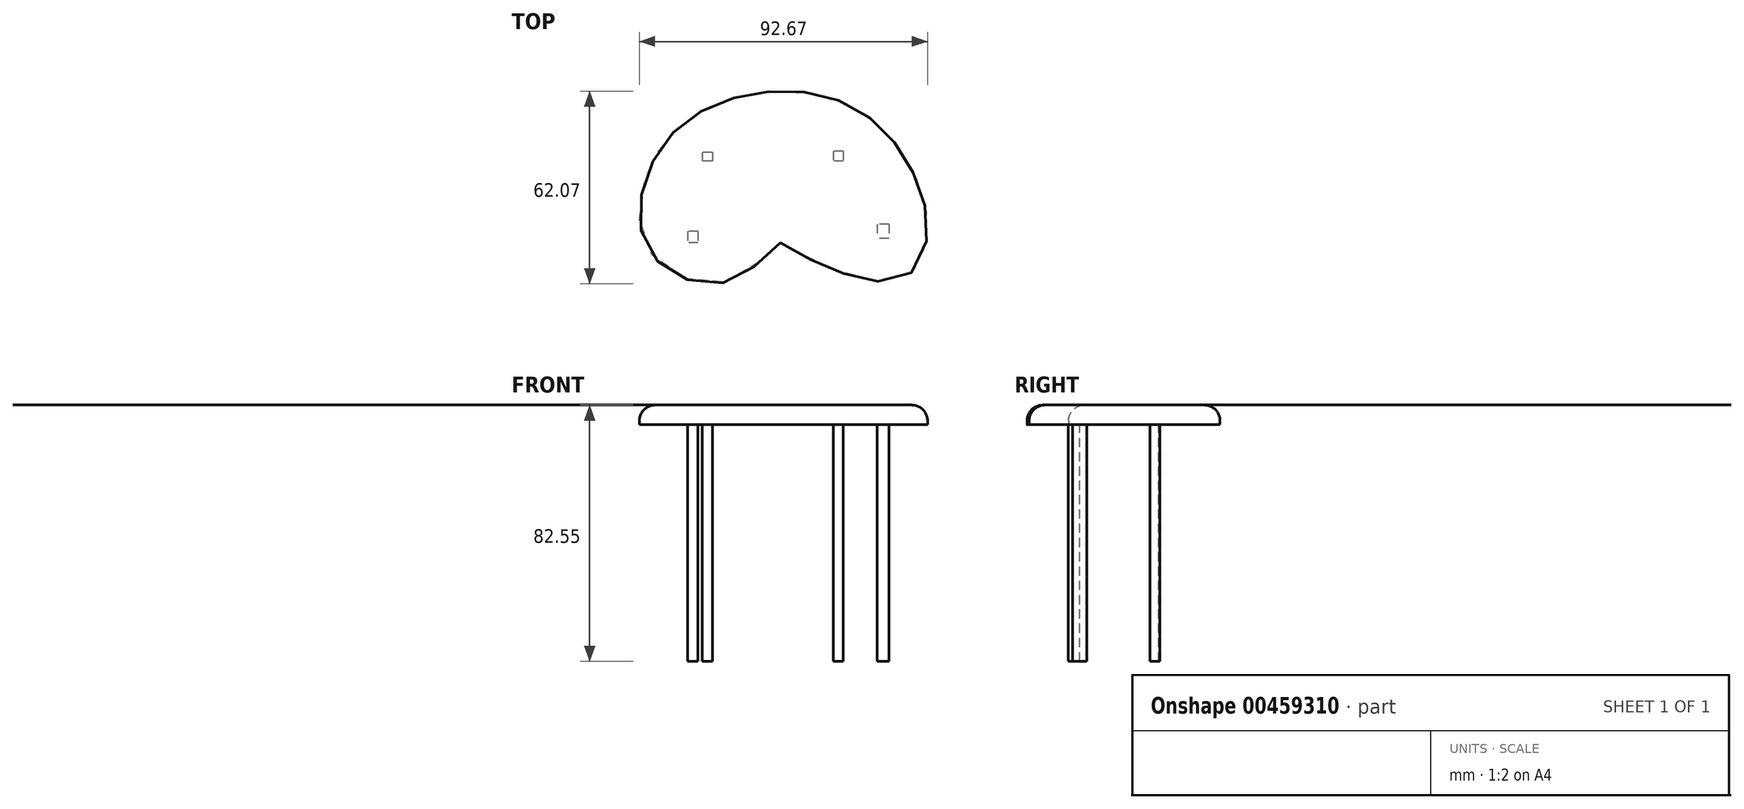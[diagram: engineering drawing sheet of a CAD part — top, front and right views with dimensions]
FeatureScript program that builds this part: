
annotation { "Feature Type Name" : "Feature", "Feature Type Description" : "" }
export const myFeature = defineFeature(function(context is Context, id is Id, definition is map)
    precondition{}
    {
        {
            var Q0;
            Q0=qCreatedBy(makeId("Top.planeOp"),FACE);
            var sketch = newSketch(context, id + "F0", { "sketchPlane" : qUnion([Q0])});
            skFitSpline(sketch, "E0", {"points": [v(0, -6.05) * mm, v(-16.28, -18.37) * mm, v(-42.1, -8.84) * mm, v(-43.26, 14.65) * mm, v(-33.5, 30.47) * mm, v(-15.35, 40.47) * mm, v(10.23, 42.1) * mm, v(30.24, 33.03) * mm, v(43.73, 14.42) * mm, v(46.98, -5.81) * mm, v(36.28, -18.37) * mm, v(4.19, -8.14) * mm, v(0, -6.05) * mm]});
            skSolve(sketch);
        }
        {
            var Q0;
            Q0 = qSketchRegion(id + "F0", true);
            extrude(context, id + "F1", {"entities" : qUnion([Q0]), "depth" : 6.35 * mm});
        }
        {
            var Q0;
            Q0=makeQuery(id+"F1.opExtrude","CAP_FACE",FACE,{"disambiguationData":[OSD([sQuery(id+"F0.wireOp",EDGE,"E0")])],"isStart":false});
            fillet(context, id + "F2", {"entities" : qUnion([Q0]), "radius" : 5.08 * mm, "tangentPropagation" : true, "allowEdgeOverflow" : false});
        }
        {
            var Q0;
            Q0=qCreatedBy(makeId("Top.planeOp"),FACE);
            var sketch = newSketch(context, id + "F3", { "sketchPlane" : qUnion([Q0])});
            skLineSegment(sketch, "E1.bottom", {"start": v(-26.51, -2.33) * mm, "end": v(-29.77, -2.33) * mm});
            skLineSegment(sketch, "E1.top", {"start": v(-26.51, -6.05) * mm, "end": v(-29.77, -6.05) * mm});
            skLineSegment(sketch, "E1.left", {"start": v(-26.51, -2.33) * mm, "end": v(-26.51, -6.05) * mm});
            skLineSegment(sketch, "E1.right", {"start": v(-29.77, -2.33) * mm, "end": v(-29.77, -6.05) * mm});
            skPoint(sketch, "E1.middle", {"position": v(-28.14, -4.19) * mm});
            skLineSegment(sketch, "E2.bottom", {"start": v(34.89, 0) * mm, "end": v(31.17, 0) * mm});
            skLineSegment(sketch, "E2.top", {"start": v(34.89, -4.65) * mm, "end": v(31.17, -4.65) * mm});
            skLineSegment(sketch, "E2.left", {"start": v(34.89, 0) * mm, "end": v(34.89, -4.65) * mm});
            skLineSegment(sketch, "E2.right", {"start": v(31.17, 0) * mm, "end": v(31.17, -4.65) * mm});
            skPoint(sketch, "E2.middle", {"position": v(33.03, -2.33) * mm});
            skLineSegment(sketch, "E3.bottom", {"start": v(-21.86, 23.03) * mm, "end": v(-25.12, 23.03) * mm});
            skLineSegment(sketch, "E3.top", {"start": v(-21.86, 20.24) * mm, "end": v(-25.12, 20.24) * mm});
            skLineSegment(sketch, "E3.left", {"start": v(-21.86, 23.03) * mm, "end": v(-21.86, 20.24) * mm});
            skLineSegment(sketch, "E3.right", {"start": v(-25.12, 23.03) * mm, "end": v(-25.12, 20.24) * mm});
            skPoint(sketch, "E3.middle", {"position": v(-23.5, 21.63) * mm});
            skLineSegment(sketch, "E4.bottom", {"start": v(20.24, 23.5) * mm, "end": v(16.98, 23.5) * mm});
            skLineSegment(sketch, "E4.top", {"start": v(20.24, 20.24) * mm, "end": v(16.98, 20.24) * mm});
            skLineSegment(sketch, "E4.left", {"start": v(20.24, 23.5) * mm, "end": v(20.24, 20.24) * mm});
            skLineSegment(sketch, "E4.right", {"start": v(16.98, 23.5) * mm, "end": v(16.98, 20.24) * mm});
            skPoint(sketch, "E4.middle", {"position": v(18.6, 21.86) * mm});
            skSolve(sketch);
        }
        {
            var Q0;
            Q0 = qSketchRegion(id + "F3", true);
            extrude(context, id + "F4", {"entities" : qUnion([Q0]), "operationType" : NewBodyOperationType.ADD, "oppositeDirection" : true, "depth" : 76.2 * mm});
        }
    });
